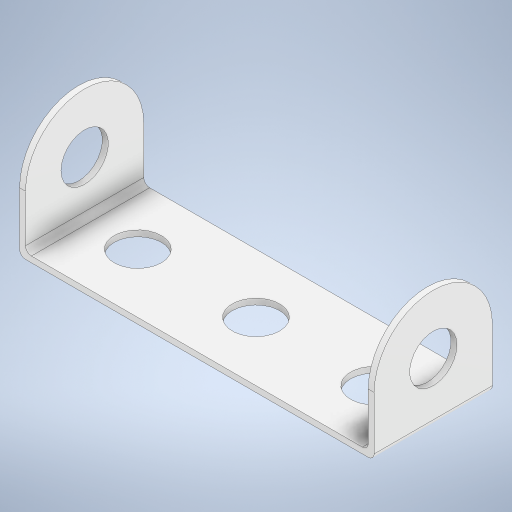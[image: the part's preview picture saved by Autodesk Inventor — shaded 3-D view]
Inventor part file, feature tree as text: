
AUTODESK INVENTOR PART (.ipt)
format: ipt  version: 2024 (Build 280153000, 153)  size: 307,712 bytes
history: native  units: mm
features: extrude x4, sketch x4, pattern_linear x2, fillet x2, other x1
ambient origin geometry x8: Origin, YZ Plane, XZ Plane, XY Plane, X Axis, Y Axis, Z Axis, Center Point
bodies: Body1 (feature_tree)
feature tree (13):
  other  "Těleso1"
  extrude  "Vysunutí1"  Depth=15.0mm
  extrude  "Vysunutí2"  Depth=15.0mm
  pattern_linear  "Obdélníkové pole1"  Spacing1=0.5mm  [1 undecoded]
  extrude  "Vysunutí3"  Depth=0.5mm
  pattern_linear  "Obdélníkové pole2"  Spacing1=0.5mm  [1 undecoded]
  extrude  "Vysunutí4"  Depth=10.0mm
  fillet  "Zaoblení1"  Radius=10.0mm
  fillet  "Zaoblení2"  Radius=10.0mm
  sketch  "Náčrt1"
  sketch  "Náčrt2"
  sketch  "Náčrt3"
  sketch  "Náčrt4"
note: 2 required parameter values undecoded (feature->parameter linkage not recoverable at this tier; creation-order binding heuristic only, values carry confidence <= 0.55)
